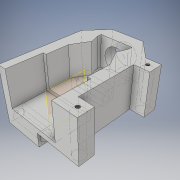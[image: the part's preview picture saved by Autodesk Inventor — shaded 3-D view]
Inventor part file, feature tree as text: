
AUTODESK INVENTOR PART (.ipt)
format: ipt  version: 2019 (Build 230136000, 136)  size: 386,560 bytes
history: native  units: mm
features: extrude x20, sketch x20, projected_geometry x8, chamfer x2, plane x1, mirror x1
ambient origin geometry x8: Origin, YZ Plane, XZ Plane, XY Plane, X Axis, Y Axis, Z Axis, Center Point
bodies: Solid1 (feature_tree)
feature tree (52):
  extrude  "Extrusion1"  Depth=13.0mm
  extrude  "Extrusion2"  Depth=13.0mm
  extrude  "Extrusion3"  Depth=7.0mm TaperAngle=0.0deg
  extrude  "Extrusion4"  Depth=5.2mm
  extrude  "Extrusion5"  Depth=5.0mm TaperAngle=0.0deg
  extrude  "Extrusion6"  Depth=21.3mm TaperAngle=0.0deg
  extrude  "Extrusion7"  Depth=2.0mm
  extrude  "Extrusion8"  Depth=2.0mm
  extrude  "Extrusion9"  Depth=5.0mm
  extrude  "Extrusion10"  Depth=2.0mm TaperAngle=0.0deg
  extrude  "Extrusion11"  Depth=2.5mm
  extrude  "Extrusion12"  Depth=5.0mm TaperAngle=0.0deg
  extrude  "Extrusion13"  Depth=8.3mm
  plane  "Work Plane1"
  mirror  "Mirror1"
  extrude  "Extrusion14"  Depth=21.3mm TaperAngle=0.0deg
  extrude  "Extrusion20"  Depth=21.3mm TaperAngle=0.0deg
  chamfer  "Chamfer2"  Distance=21.3mm
  extrude  "Extrusion22"  Depth=2.0mm
  extrude  "Extrusion23"  Depth=2.0mm
  chamfer  "Chamfer3"  Distance=19.2mm
  extrude  "Extrusion24"  Depth=8.0mm
  extrude  "Extrusion25"  Depth=8.0mm
  extrude  "Extrusion26"  Depth=2.0mm
  sketch  "Sketch1"  dims[d0=25.32mm d1=13.0mm]
  sketch  "Sketch2"  dims[d2=5.0mm d3=0.0mm d4=13.0mm]
  sketch  "Sketch3"  dims[d5=21.3mm d6=7.0mm d7=0.0mm]
  sketch  "Sketch4"  dims[d8=10.0mm d9=5.2mm]
  sketch  "Sketch5"  dims[d10=5.2mm d11=5.0mm d12=0.0mm]
  sketch  "Sketch6"  dims[d13=7.2mm d14=21.3mm d15=0.0mm]
  sketch  "Sketch7"  dims[d16=5.9mm d17=2.0mm]
  sketch  "Sketch8"  dims[d18=2.0mm d19=2.0mm]
  sketch  "Sketch9"  dims[d20=5.0mm d21=0.0mm d22=5.9mm]
  sketch  "Sketch10"  dims[d23=2.0mm d24=21.3mm d25=0.0mm]
  sketch  "Sketch11"  dims[d26=2.5mm d27=2.5mm]
  sketch  "Sketch12"  dims[d28=5.0mm d29=0.0mm d30=21.3mm d31=0.0mm]
  sketch  "Sketch13"  dims[d32=18.92mm d33=8.3mm]
  sketch  "Sketch16"  dims[d34=21.3mm d35=0.0mm d36=21.3mm d37=0.0mm]
  sketch  "Sketch22"  dims[d38=13.25mm d39=21.3mm d40=0.0mm d41=21.3mm d42=0.0mm]
  sketch  "Sketch24"  dims[d43=21.3mm d44=0.0mm d45=2.0mm]
  sketch  "Sketch25"  dims[d46=2.0mm d47=2.0mm]
  sketch  "Sketch26"  dims[d48=2.0mm d49=19.2mm d50=0.0mm]
  projected_geometry  "Projected Loop1"
  projected_geometry  "Projected Loop2"
  sketch  "Sketch28"  dims[d81=8.0mm d82=8.0mm]
  projected_geometry  "Projected Loop3"
  projected_geometry  "Projected Loop4"
  sketch  "Sketch29"  dims[d83=8.0mm d84=8.0mm d85=2.0mm d86=2.0mm d87=2.5mm d88=0.0mm d89=2.0mm d90=2.0mm d91=45.0deg d94=2.0mm d95=0.0mm d96=8.0mm d97=8.0mm d98=8.0mm d99=8.0mm d100=2.0mm d101=2.0mm d102=2.0mm d103=0.0mm d104=2.0mm d105=2.0mm d106=45.0deg d107=21.3mm d108=0.0mm d109=21.3mm d110=0.0mm d111=20.0mm d112=0.0mm]
  projected_geometry  "Projected Loop5"
  projected_geometry  "Projected Loop6"
  projected_geometry  "Projected Loop7"
  projected_geometry  "Projected Loop8"
